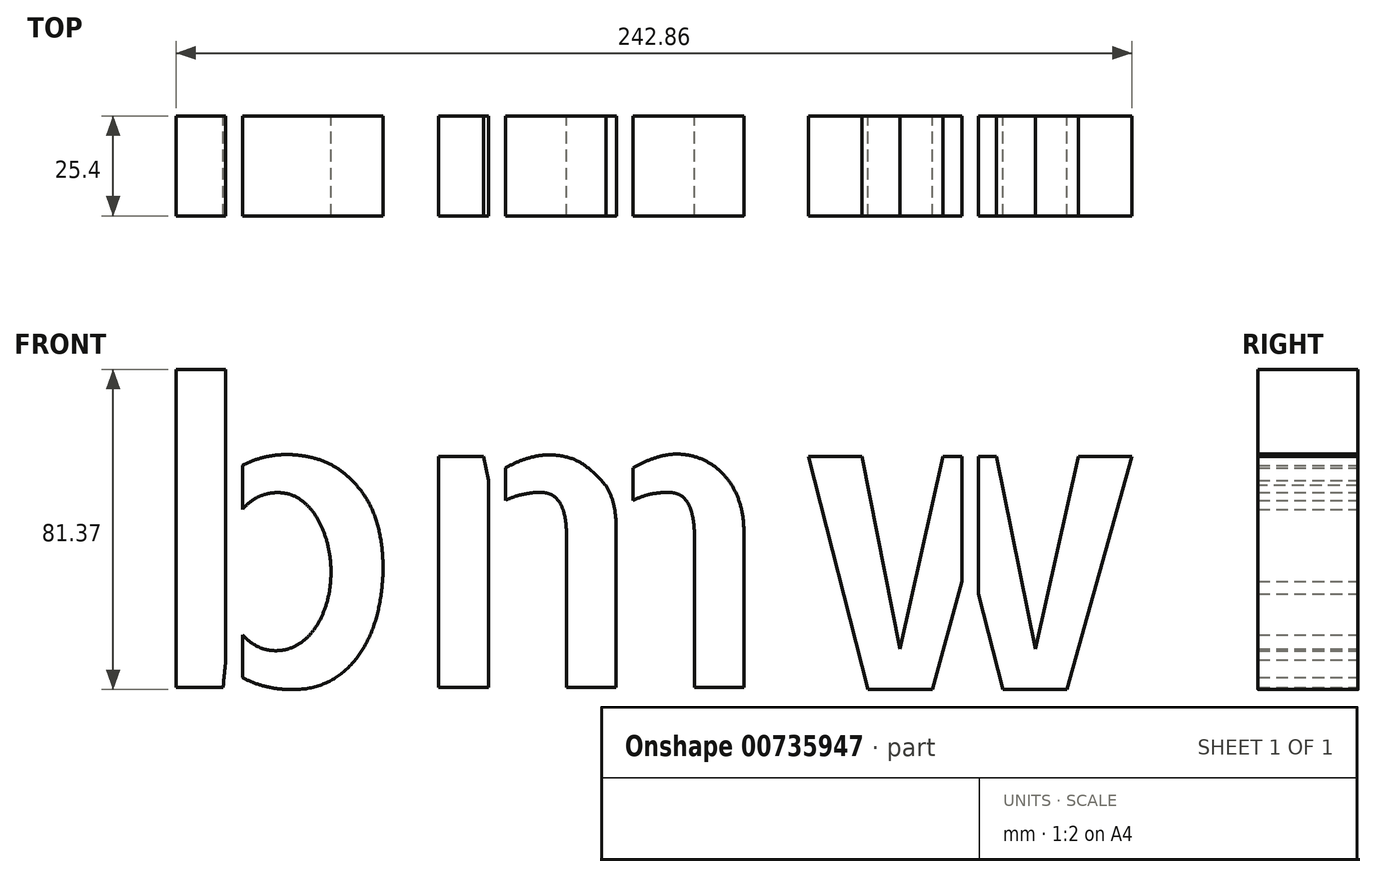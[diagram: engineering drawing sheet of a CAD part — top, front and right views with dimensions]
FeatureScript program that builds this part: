
annotation { "Feature Type Name" : "Feature", "Feature Type Description" : "" }
export const myFeature = defineFeature(function(context is Context, id is Id, definition is map)
    precondition{}
    {
        {
            var Q0;
            Q0=qCreatedBy(makeId("Front.planeOp"),FACE);
            var sketch = newSketch(context, id + "F0", { "sketchPlane" : qUnion([Q0])});
            skText(sketch, "E0", { "text": "bmw", "fontName": "AllertaStencil-Regular.ttf"});
            const initialGuessF0  = {"E0": [-0.0523, -0.03234, 1, 0, 0.07672]};
            skSetInitialGuess(sketch, initialGuessF0);
            skSolve(sketch);
        }
        {
            var Q0;
            Q0=makeQuery(id+"F0.imprint","IMPRINT",FACE,{"disambiguationData":[TD([[makeQuery(id+"F0.imprint","IMPRINT",EDGE,{"derivedFrom":sQuery(id+"F0.wireOp",EDGE,"E0.sketch_text.stroke-0")}),-1.0]])]});
            var Q1;
            Q1=makeQuery(id+"F0.imprint","IMPRINT",FACE,{"disambiguationData":[TD([[makeQuery(id+"F0.imprint","IMPRINT",EDGE,{"derivedFrom":sQuery(id+"F0.wireOp",EDGE,"E0.sketch_text.stroke-6")}),-1.0]])]});
            var Q2;
            Q2=makeQuery(id+"F0.imprint","IMPRINT",FACE,{"disambiguationData":[TD([[makeQuery(id+"F0.imprint","IMPRINT",EDGE,{"derivedFrom":sQuery(id+"F0.wireOp",EDGE,"E0.sketch_text.stroke-33")}),-1.0]])]});
            var Q3;
            Q3=makeQuery(id+"F0.imprint","IMPRINT",FACE,{"disambiguationData":[TD([[makeQuery(id+"F0.imprint","IMPRINT",EDGE,{"derivedFrom":sQuery(id+"F0.wireOp",EDGE,"E0.sketch_text.stroke-54")}),-1.0]])]});
            var Q4;
            Q4=makeQuery(id+"F0.imprint","IMPRINT",FACE,{"disambiguationData":[TD([[makeQuery(id+"F0.imprint","IMPRINT",EDGE,{"derivedFrom":sQuery(id+"F0.wireOp",EDGE,"E0.sketch_text.stroke-80")}),-1.0]])]});
            var Q5;
            Q5=makeQuery(id+"F0.imprint","IMPRINT",FACE,{"disambiguationData":[TD([[makeQuery(id+"F0.imprint","IMPRINT",EDGE,{"derivedFrom":sQuery(id+"F0.wireOp",EDGE,"E0.sketch_text.stroke-38")}),-1.0]])]});
            var Q6;
            Q6=makeQuery(id+"F0.imprint","IMPRINT",FACE,{"disambiguationData":[TD([[makeQuery(id+"F0.imprint","IMPRINT",EDGE,{"derivedFrom":sQuery(id+"F0.wireOp",EDGE,"E0.sketch_text.stroke-72")}),-1.0]])]});
            extrude(context, id + "F1", {"entities" : qUnion([Q0, Q1, Q2, Q3, Q4, Q5, Q6]), "depth" : 25.4 * mm, "offsetDistance" : 25.4 * mm});
        }
    });
